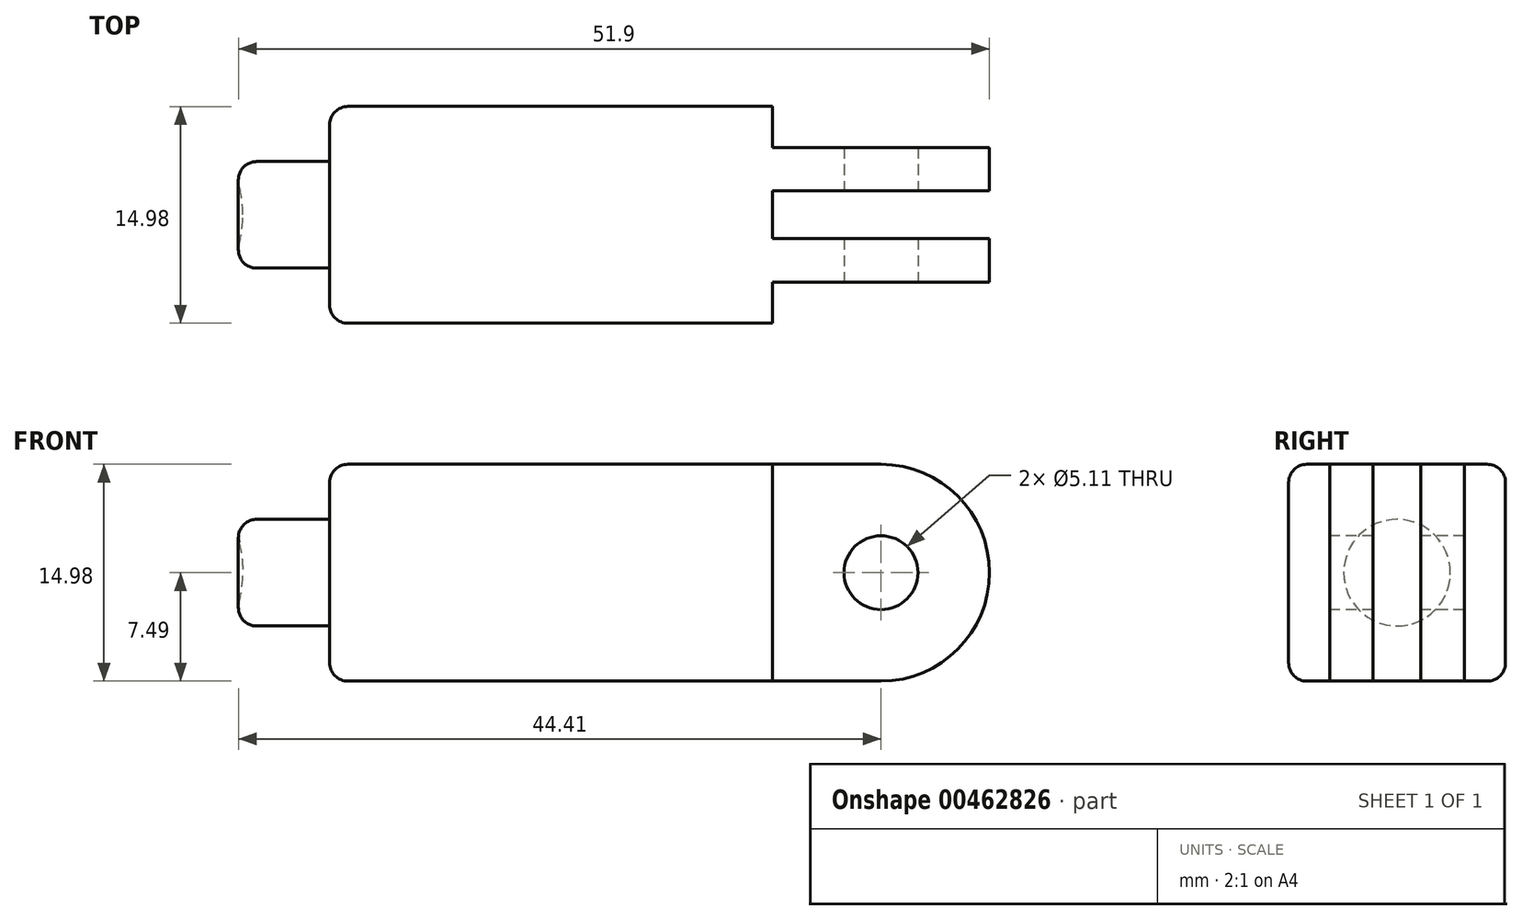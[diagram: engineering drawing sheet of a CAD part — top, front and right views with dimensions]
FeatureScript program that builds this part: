
annotation { "Feature Type Name" : "Feature", "Feature Type Description" : "" }
export const myFeature = defineFeature(function(context is Context, id is Id, definition is map)
    precondition{}
    {
        {
            var Q0;
            Q0=qCreatedBy(makeId("Front.planeOp"),FACE);
            var sketch = newSketch(context, id + "F0", { "sketchPlane" : qUnion([Q0])});
            skLineSegment(sketch, "E0.bottom", {"start": v(19.05, -7.5) * mm, "end": v(-19.05, -7.5) * mm});
            skLineSegment(sketch, "E0.top", {"start": v(19.05, 7.5) * mm, "end": v(-19.05, 7.5) * mm});
            skLineSegment(sketch, "E0.left", {"start": v(19.05, -7.5) * mm, "end": v(19.05, 7.5) * mm});
            skLineSegment(sketch, "E0.right", {"start": v(-19.05, -7.5) * mm, "end": v(-19.05, 7.5) * mm});
            skPoint(sketch, "E0.middle", {"position": v(0, 0) * mm});
            skCircle(sketch, "E1", {"center": v(19.05, 0) * mm, "radius": 7.5 * mm});
            skSolve(sketch);
        }
        {
            var Q0;
            Q0=makeQuery(id+"F0.imprint","IMPRINT",FACE,{"disambiguationData":[TD([[makeQuery(id+"F0.imprint","IMPRINT",EDGE,{"derivedFrom":sQuery(id+"F0.wireOp",EDGE,"E0.bottom")}),-1.0]])]});
            var Q1;
            {var subQ0=sQuery(id+"F0.wireOp",EDGE,"E0.left");Q1=makeQuery(id+"F0.imprint","IMPRINT",FACE,{"disambiguationData":[TD([[makeQuery(id+"F0.imprint","IMPRINT",EDGE,{"derivedFrom":subQ0}),1.0]])]});}
            var Q2;
            {var subQ0=sQuery(id+"F0.wireOp",EDGE,"E0.left");Q2=makeQuery(id+"F0.imprint","IMPRINT",FACE,{"disambiguationData":[TD([[makeQuery(id+"F0.imprint","IMPRINT",EDGE,{"derivedFrom":subQ0}),-1.0]])]});}
            extrude(context, id + "F1", {"entities" : qUnion([Q0, Q1, Q2]), "depth" : 7.5 * mm, "hasSecondDirection" : true, "secondDirectionOppositeDirection" : true, "secondDirectionDepth" : 7.5 * mm});
        }
        {
            var Q0;
            Q0=makeQuery(id+"F1.opExtrude","CAP_FACE",FACE,{"disambiguationData":[OSD([sQuery(id+"F0.wireOp",EDGE,"E0.bottom"),sQuery(id+"F0.wireOp",EDGE,"E0.top"),sQuery(id+"F0.wireOp",EDGE,"E0.right"),sQuery(id+"F0.wireOp",EDGE,"E1")])],"isStart":false});
            var sketch = newSketch(context, id + "F2", { "sketchPlane" : qUnion([Q0])});
            skPoint(sketch, "E2", {"position": v(19.05, 0) * mm});
            skSolve(sketch);
        }
        {
            var Q0;
            Q0=sQuery(id+"F2.wireOp",VERTEX,"E2");
            var Q1;
            Q1=makeQuery(id+"F1.opExtrude","SWEPT_BODY",BODY,{"disambiguationData":[OSD([sQuery(id+"F0.wireOp",EDGE,"E0.bottom"),sQuery(id+"F0.wireOp",EDGE,"E0.top"),sQuery(id+"F0.wireOp",EDGE,"E0.right"),sQuery(id+"F0.wireOp",EDGE,"E1")])]});
            hole(context, id + "F3", {"style" : HoleStyle.SIMPLE, "endStyle" : HoleEndStyle.THROUGH, "standardTappedOrClearance" : lookupTablePath({ "standard" : "ANSI", "fit" : "Normal (ASME)", "size" : "#10", "type" : "Clearance" }), "standardBlindInLast" : lookupTablePath({ "fit" : "Free", "standard" : "ANSI", "size" : "#10", "type" : "Clearance" }), "holeDiameter" : 5.1 * mm, "tappedDepth" : 12.7 * mm, "tapClearance" : 3, "startFromSketch" : true, "locations" : qUnion([Q0]), "scope" : qUnion([Q1])});
        }
        {
            var Q0;
            Q0=makeQuery(id+"F1.opExtrude","SWEPT_FACE",FACE,{"disambiguationData":[OSD([sQuery(id+"F0.wireOp",EDGE,"E0.top")])]});
            var sketch = newSketch(context, id + "F4", { "sketchPlane" : qUnion([Q0])});
            skLineSegment(sketch, "E3.bottom", {"start": v(11.56, 7.5) * mm, "end": v(26.54, 7.5) * mm});
            skLineSegment(sketch, "E3.top", {"start": v(11.56, 4.65) * mm, "end": v(26.54, 4.65) * mm});
            skLineSegment(sketch, "E3.left", {"start": v(11.56, 7.5) * mm, "end": v(11.56, 4.65) * mm});
            skLineSegment(sketch, "E3.right", {"start": v(26.54, 7.5) * mm, "end": v(26.54, 4.65) * mm});
            skLineSegment(sketch, "E4.bottom", {"start": v(11.56, 1.65) * mm, "end": v(26.54, 1.65) * mm});
            skLineSegment(sketch, "E4.top", {"start": v(11.56, -1.65) * mm, "end": v(26.54, -1.65) * mm});
            skLineSegment(sketch, "E4.left", {"start": v(11.56, 1.65) * mm, "end": v(11.56, -1.65) * mm});
            skLineSegment(sketch, "E4.right", {"start": v(26.54, 1.65) * mm, "end": v(26.54, -1.65) * mm});
            skLineSegment(sketch, "E5.bottom", {"start": v(11.56, -4.65) * mm, "end": v(26.54, -4.65) * mm});
            skLineSegment(sketch, "E5.top", {"start": v(11.56, -7.5) * mm, "end": v(26.54, -7.5) * mm});
            skLineSegment(sketch, "E5.left", {"start": v(11.56, -4.65) * mm, "end": v(11.56, -7.5) * mm});
            skLineSegment(sketch, "E5.right", {"start": v(26.54, -4.65) * mm, "end": v(26.54, -7.5) * mm});
            skLineSegment(sketch, "E6", {"start": v(0, 0) * mm, "end": v(5.48, 0) * mm});
            skSolve(sketch);
        }
        {
            var Q0;
            {var subQ4=sQuery(id+"F4.wireOp",EDGE,"E3.left");Q0=makeQuery(id+"F4.imprint","IMPRINT",FACE,{"disambiguationData":[TD([[makeQuery(id+"F4.imprint","IMPRINT",EDGE,{"derivedFrom":subQ4}),1.0]])]});}
            var Q1;
            {var subQ3=sQuery(id+"F4.wireOp",EDGE,"E3.right");Q1=makeQuery(id+"F4.imprint","IMPRINT",FACE,{"disambiguationData":[TD([[makeQuery(id+"F4.imprint","IMPRINT",EDGE,{"derivedFrom":subQ3}),-1.0]])]});}
            var Q2;
            {var subQ0=sQuery(id+"F4.wireOp",EDGE,"E4.right");Q2=makeQuery(id+"F4.imprint","IMPRINT",FACE,{"disambiguationData":[TD([[makeQuery(id+"F4.imprint","IMPRINT",EDGE,{"derivedFrom":subQ0}),-1.0]])]});}
            var Q3;
            {var subQ0=sQuery(id+"F4.wireOp",EDGE,"E4.left");Q3=makeQuery(id+"F4.imprint","IMPRINT",FACE,{"disambiguationData":[TD([[makeQuery(id+"F4.imprint","IMPRINT",EDGE,{"derivedFrom":subQ0}),1.0]])]});}
            var Q4;
            {var subQ0=sQuery(id+"F4.wireOp",EDGE,"E5.left");Q4=makeQuery(id+"F4.imprint","IMPRINT",FACE,{"disambiguationData":[TD([[makeQuery(id+"F4.imprint","IMPRINT",EDGE,{"derivedFrom":subQ0}),1.0]])]});}
            var Q5;
            {var subQ0=sQuery(id+"F4.wireOp",EDGE,"E5.right");Q5=makeQuery(id+"F4.imprint","IMPRINT",FACE,{"disambiguationData":[TD([[makeQuery(id+"F4.imprint","IMPRINT",EDGE,{"derivedFrom":subQ0}),-1.0]])]});}
            extrude(context, id + "F5", {"entities" : qUnion([Q0, Q1, Q2, Q3, Q4, Q5]), "operationType" : NewBodyOperationType.REMOVE, "oppositeDirection" : true, "depth" : 25.4 * mm});
        }
        {
            var Q0;
            Q0=qCreatedBy(makeId("Front.planeOp"),FACE);
            var sketch = newSketch(context, id + "F6", { "sketchPlane" : qUnion([Q0])});
            skLineSegment(sketch, "E7", {"start": v(-19.05, 0) * mm, "end": v(-41.82, 0) * mm});
            skArc(sketch, "E8", {"start": v(-25.06, 0) * mm, "mid": v(-33.44, 8.38) * mm, "end": v(-41.82, 0) * mm});
            skLineSegment(sketch, "E9", {"start": v(-25.9, 3.68) * mm, "end": v(-19.05, 3.68) * mm});
            skLineSegment(sketch, "E10", {"start": v(-19.05, 3.68) * mm, "end": v(-19.05, 0) * mm});
            skSolve(sketch);
        }
        {
            var Q0;
            {var subQ0=sQuery(id+"F6.wireOp",EDGE,"E8");var subQ1=sQuery(id+"F6.wireOp",EDGE,"E7");var subQ2=makeQuery(id+"F6.imprint","INTERSECT",VERTEX,{"disambiguationData":[OD(0.0)],"derivedFrom":[subQ1,subQ0]});Q0=makeQuery(id+"F6.imprint","IMPRINT",FACE,{"disambiguationData":[TD([[makeQuery(id+"F6.imprint","IMPRINT",EDGE,{"disambiguationData":[TD([[subQ2,1.0]])],"derivedFrom":subQ1}),-1.0]])]});}
            var Q1;
            {var subQ4=sQuery(id+"F6.wireOp",EDGE,"E9");Q1=makeQuery(id+"F6.imprint","IMPRINT",FACE,{"disambiguationData":[TD([[makeQuery(id+"F6.imprint","IMPRINT",EDGE,{"derivedFrom":subQ4}),-1.0]])]});}
            var Q2;
            Q2=sQuery(id+"F6.wireOp",EDGE,"E7");
            revolve(context, id + "F7", {"operationType" : NewBodyOperationType.ADD, "entities" : qUnion([Q0, Q1]), "axis" : qUnion([Q2]), "revolveType" : RevolveType.FULL});
        }
        {
            var Q0;
            Q0=makeQuery(id+"F7.opRevolve","SWEPT_EDGE",EDGE,{"disambiguationData":[OSD([sQuery(id+"F6.wireOp",EDGE,"E8"),sQuery(id+"F6.wireOp",EDGE,"E9")])]});
            var Q1;
            Q1=makeQuery(id+"F7.opRevolve","SWEPT_EDGE",EDGE,{"disambiguationData":[OSD([sQuery(id+"F6.wireOp",EDGE,"E9"),sQuery(id+"F6.wireOp",EDGE,"E10")])]});
            fillet(context, id + "F8", {"entities" : qUnion([Q0, Q1]), "radius" : 1.27 * mm, "tangentPropagation" : true, "allowEdgeOverflow" : false});
        }
        {
            var Q0;
            Q0=makeQuery(id+"F1.opExtrude","CAP_EDGE",EDGE,{"disambiguationData":[OSD([sQuery(id+"F0.wireOp",EDGE,"E0.right")])],"isStart":false});
            var Q1;
            Q1=makeQuery(id+"F1.opExtrude","SWEPT_EDGE",EDGE,{"disambiguationData":[OSD([sQuery(id+"F0.wireOp",EDGE,"E0.top"),sQuery(id+"F0.wireOp",EDGE,"E0.right")])]});
            var Q2;
            Q2=makeQuery(id+"F1.opExtrude","CAP_EDGE",EDGE,{"disambiguationData":[OSD([sQuery(id+"F0.wireOp",EDGE,"E0.top")])],"isStart":false});
            var Q3;
            Q3=makeQuery(id+"F1.opExtrude","CAP_EDGE",EDGE,{"disambiguationData":[OSD([sQuery(id+"F0.wireOp",EDGE,"E0.top")])],"isStart":true});
            var Q4;
            Q4=makeQuery(id+"F1.opExtrude","CAP_EDGE",EDGE,{"disambiguationData":[OSD([sQuery(id+"F0.wireOp",EDGE,"E0.right")])],"isStart":true});
            var Q5;
            Q5=makeQuery(id+"F1.opExtrude","SWEPT_EDGE",EDGE,{"disambiguationData":[OSD([sQuery(id+"F0.wireOp",EDGE,"E0.bottom"),sQuery(id+"F0.wireOp",EDGE,"E0.right")])]});
            var Q6;
            Q6=makeQuery(id+"F1.opExtrude","CAP_EDGE",EDGE,{"disambiguationData":[OSD([sQuery(id+"F0.wireOp",EDGE,"E0.bottom")])],"isStart":true});
            var Q7;
            Q7=makeQuery(id+"F1.opExtrude","CAP_EDGE",EDGE,{"disambiguationData":[OSD([sQuery(id+"F0.wireOp",EDGE,"E0.bottom")])],"isStart":false});
            fillet(context, id + "F9", {"entities" : qUnion([Q0, Q1, Q2, Q3, Q4, Q5, Q6, Q7]), "radius" : 1.27 * mm, "tangentPropagation" : true, "allowEdgeOverflow" : false});
        }
    });
